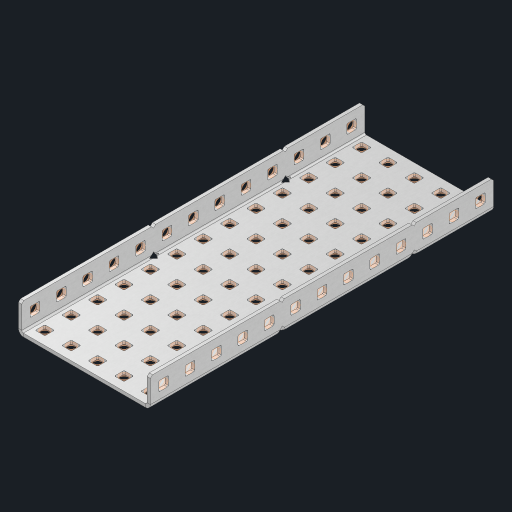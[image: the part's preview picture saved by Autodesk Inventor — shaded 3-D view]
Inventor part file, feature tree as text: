
AUTODESK INVENTOR PART (.ipt)
format: ipt  version: 2023 (Build 270158000, 158)  size: 1,217,024 bytes
history: native  units: in
note: dims shown in document units (in); Inventor stores cm internally (conversion verified against a paired STEP export)
features: other x96, extrude x90, sheet_metal_op x10, sketch x8, mirror x1, pattern_linear x1, chamfer x1
ambient origin geometry x8: Origin, YZ Plane, XZ Plane, XY Plane, X Axis, Y Axis, Z Axis, Center Point
bodies: Solid1 (feature_tree), Body (feature_tree)
feature tree (207):
  other  "Flange Pattern Plane"
  sheet_metal_op  "Flange Pattern"
  sheet_metal_op  "Body Pattern"
  other  "Arc Length"
  mirror  "Notch Mirror"
  pattern_linear  "Notch Pattern"  Spacing1=0.25in  [1 undecoded]
  chamfer  "End Chamfer"
  extrude  "Half Cut"  Depth=0.0625in
  sketch  "Sketch1"  dims[d0=2.5in]
  other  "Plate1"
  sketch  "Sketch2"  dims[d1=6.5in]
  other  "Plate2"
  sheet_metal_op  "Bend1"
  sheet_metal_op  "Corner1"
  sketch  "Sketch3"  dims[d2=0.0625in]
  other  "Flange Pattern Sketch"
  sketch  "Sketch7"  dims[d3=0.0625in]
  other  "Srf1"
  other  "Srf2"
  sketch  "Sketch8"  dims[d4=0.0312in]
  sketch  "Sketch9"  dims[d5=0.125in]
  other  "Srf91"
  sheet_metal_op  "Body Pattern Sketch"
  other  "Srf92"
  sketch  "Sketch13"  dims[d6=0.0625in]
  sketch  "Sketch14"  dims[d7=0.5in d8=90.0deg d9=0.0312in d10=0.25in d11=0.0625in d12=0.0625in d16=0.182in d17=0.02in d18=0.0625in d19=0.0in d20=0.25in d21=0.25in d46=0.172in d47=1.0in d48=0.0in d49=0.182in d50=0.02in d51=0.25in d52=0.25in d53=0.0625in d54=0.0in d55=0.172in d56=1.0in d57=0.0in d60=5.1181in d62=0.5in d63=1.9685in d65=0.5in d85=0.1473in d86=0.1782in d88=0.04in d89=0.0625in d90=0.0in d91=0.04in d92=0.0491in d95=2.5in d96=0.04in d97=0.25in d98=45.0deg d101=0.0in d102=2.497in d131=2.5in d132=5.1181in d134=0.5in d139=0.5in]
  other  "Srf856"
  other  "Srf1310"
  other  "Srf1311"
  other  "Srf1312"
  other  "Srf1376"
  other  "Srf1377"
  other  "Srf1728"
  other  "Srf1755"
  other  "Srf1878"
  other  "Srf1879"
  other  "Srf1880"
  other  "Srf1881"
  other  "Srf1882"
  other  "Srf1883"
  other  "Srf1884"
  other  "Srf1885"
  other  "Srf1886"
  other  "Srf1887"
  other  "Srf1888"
  other  "Srf1889"
  other  "Srf1890"
  other  "Srf1891"
  other  "Srf1892"
  other  "Srf1893"
  other  "Srf1894"
  other  "Srf1895"
  other  "Srf1896"
  other  "Srf1897"
  other  "Srf1942"
  other  "Srf1943"
  other  "Srf1944"
  other  "Srf1945"
  other  "Srf1946"
  other  "Srf1947"
  other  "Srf1948"
  other  "Srf1949"
  other  "Srf1950"
  other  "Srf1951"
  other  "Srf1952"
  other  "Srf1953"
  other  "Srf1954"
  other  "Srf1955"
  other  "Srf1956"
  other  "Srf1957"
  other  "Srf1958"
  other  "Srf1959"
  other  "Srf1960"
  other  "Srf1961"
  other  "Srf1962"
  other  "Srf1963"
  other  "Srf1964"
  other  "Srf1965"
  other  "Srf1966"
  other  "Srf1967"
  other  "Srf1968"
  other  "Srf1969"
  other  "Srf1970"
  other  "Srf2146"
  other  "Srf2147"
  other  "Srf2148"
  other  "Srf2149"
  other  "Srf2150"
  other  "Srf2151"
  other  "Srf2152"
  other  "Srf2153"
  other  "Srf2154"
  other  "Srf2155"
  other  "Srf2156"
  other  "Srf2157"
  other  "Srf2158"
  other  "Srf2159"
  other  "Srf2160"
  other  "Srf2161"
  other  "Srf2162"
  other  "Srf2163"
  other  "Srf2164"
  other  "Srf2165"
  other  "Srf2166"
  other  "Srf2167"
  other  "Srf2168"
  other  "Srf2169"
  other  "Srf2170"
  other  "Srf2171"
  other  "Srf2172"
  other  "Srf2173"
  other  "Srf2174"
  other  "Srf2175"
  sheet_metal_op  "Flange Stamp"
  sheet_metal_op  "Flange Circle"
  sheet_metal_op  "Body Stamp"
  sheet_metal_op  "Body Circle"
  sheet_metal_op  "Notch"
  extrude  "ExtrusionSrf2"  Depth=0.0625in
  extrude  "ExtrusionSrf92"  Depth=2.5in
  extrude  "ExtrusionSrf856"  Depth=0.02in
  extrude  "ExtrusionSrf1310"  Depth=0.0625in
  extrude  "ExtrusionSrf1311"  TaperAngle=0.0deg  [1 undecoded]
  extrude  "ExtrusionSrf1312"  Depth=0.25in
  extrude  "ExtrusionSrf1376"  Depth=0.25in
  extrude  "ExtrusionSrf1377"  Depth=2.5in
  extrude  "ExtrusionSrf1728"  Depth=2.5in TaperAngle=0.0deg
  extrude  "ExtrusionSrf1755"  Depth=2.5in
  extrude  "ExtrusionSrf1878"  Depth=0.02in
  extrude  "ExtrusionSrf1879"  Depth=0.25in
  extrude  "ExtrusionSrf1880"  Depth=0.25in
  extrude  "ExtrusionSrf1881"  Depth=0.0625in
  extrude  "ExtrusionSrf1882"  TaperAngle=0.0deg  [1 undecoded]
  extrude  "ExtrusionSrf1883"  Depth=2.5in
  extrude  "ExtrusionSrf1884"  Depth=2.5in TaperAngle=0.0deg
  extrude  "ExtrusionSrf1885"  Depth=2.5in
  extrude  "ExtrusionSrf1886"  Depth=2.5in
  extrude  "ExtrusionSrf1887"  Depth=2.5in
  extrude  "ExtrusionSrf1888"  Depth=2.5in
  extrude  "ExtrusionSrf1889"  Depth=2.5in
  extrude  "ExtrusionSrf1890"  Depth=0.0625in
  extrude  "ExtrusionSrf1891"  TaperAngle=0.0deg  [1 undecoded]
  extrude  "ExtrusionSrf1892"  Depth=2.5in
  extrude  "ExtrusionSrf1893"  Depth=2.5in
  extrude  "ExtrusionSrf1894"  Depth=2.5in
  extrude  "ExtrusionSrf1895"  Depth=0.25in TaperAngle=45.0deg
  extrude  "ExtrusionSrf1896"  TaperAngle=0.0deg  [1 undecoded]
  extrude  "ExtrusionSrf1897"  Depth=2.5in
  extrude  "ExtrusionSrf1942"  Depth=2.5in
  extrude  "ExtrusionSrf1943"  Depth=2.5in
  extrude  "ExtrusionSrf1944"  Depth=2.5in
  extrude  "ExtrusionSrf1945"  Depth=2.5in
  extrude  "ExtrusionSrf1946"  [1 undecoded]
  extrude  "ExtrusionSrf1947"  [1 undecoded]
  extrude  "ExtrusionSrf1948"  [1 undecoded]
  extrude  "ExtrusionSrf1949"  [1 undecoded]
  extrude  "ExtrusionSrf1950"  [1 undecoded]
  extrude  "ExtrusionSrf1951"  [1 undecoded]
  extrude  "ExtrusionSrf1952"  [1 undecoded]
  extrude  "ExtrusionSrf1953"  [1 undecoded]
  extrude  "ExtrusionSrf1954"  [1 undecoded]
  extrude  "ExtrusionSrf1955"  [1 undecoded]
  extrude  "ExtrusionSrf1956"  [1 undecoded]
  extrude  "ExtrusionSrf1957"  [1 undecoded]
  extrude  "ExtrusionSrf1958"  [1 undecoded]
  extrude  "ExtrusionSrf1959"  [1 undecoded]
  extrude  "ExtrusionSrf1960"  [1 undecoded]
  extrude  "ExtrusionSrf1961"  [1 undecoded]
  extrude  "ExtrusionSrf1962"  [1 undecoded]
  extrude  "ExtrusionSrf1963"  [1 undecoded]
  extrude  "ExtrusionSrf1964"  [1 undecoded]
  extrude  "ExtrusionSrf1965"  [1 undecoded]
  extrude  "ExtrusionSrf1966"  [1 undecoded]
  extrude  "ExtrusionSrf1967"  [1 undecoded]
  extrude  "ExtrusionSrf1968"  [1 undecoded]
  extrude  "ExtrusionSrf1969"  [1 undecoded]
  extrude  "ExtrusionSrf1970"  [1 undecoded]
  extrude  "ExtrusionSrf2146"  [1 undecoded]
  extrude  "ExtrusionSrf2147"  [1 undecoded]
  extrude  "ExtrusionSrf2148"  [1 undecoded]
  extrude  "ExtrusionSrf2149"  [1 undecoded]
  extrude  "ExtrusionSrf2150"  [1 undecoded]
  extrude  "ExtrusionSrf2151"  [1 undecoded]
  extrude  "ExtrusionSrf2152"  [1 undecoded]
  extrude  "ExtrusionSrf2153"  [1 undecoded]
  extrude  "ExtrusionSrf2154"  [1 undecoded]
  extrude  "ExtrusionSrf2155"  [1 undecoded]
  extrude  "ExtrusionSrf2156"  [1 undecoded]
  extrude  "ExtrusionSrf2157"  [1 undecoded]
  extrude  "ExtrusionSrf2158"  [1 undecoded]
  extrude  "ExtrusionSrf2159"  [1 undecoded]
  extrude  "ExtrusionSrf2160"  [1 undecoded]
  extrude  "ExtrusionSrf2161"  [1 undecoded]
  extrude  "ExtrusionSrf2162"  [1 undecoded]
  extrude  "ExtrusionSrf2163"  [1 undecoded]
  extrude  "ExtrusionSrf2164"  [1 undecoded]
  extrude  "ExtrusionSrf2165"  [1 undecoded]
  extrude  "ExtrusionSrf2166"  [1 undecoded]
  extrude  "ExtrusionSrf2167"  [1 undecoded]
  extrude  "ExtrusionSrf2168"  [1 undecoded]
  extrude  "ExtrusionSrf2169"  [1 undecoded]
  extrude  "ExtrusionSrf2170"  [1 undecoded]
  extrude  "ExtrusionSrf2171"  [1 undecoded]
  extrude  "ExtrusionSrf2172"  [1 undecoded]
  extrude  "ExtrusionSrf2173"  [1 undecoded]
  extrude  "ExtrusionSrf2174"  [1 undecoded]
  extrude  "ExtrusionSrf2175"  [1 undecoded]
note: 60 required parameter values undecoded (feature->parameter linkage not recoverable at this tier; creation-order binding heuristic only, values carry confidence <= 0.55)
